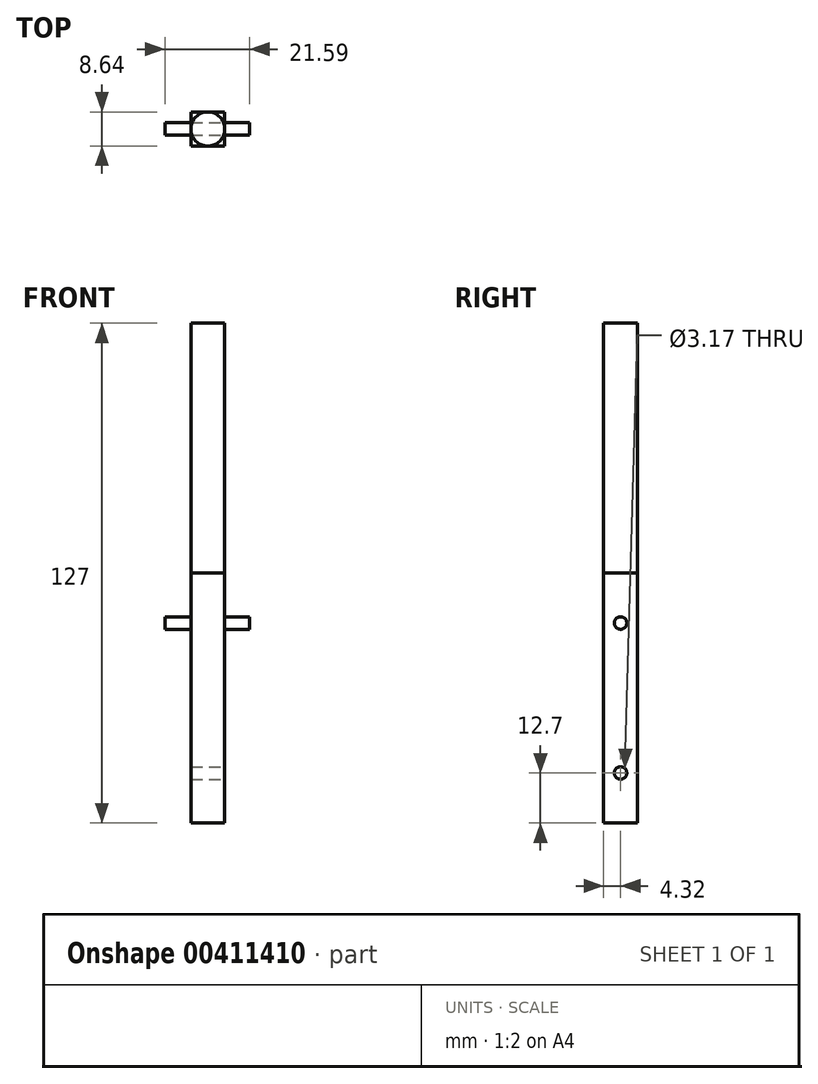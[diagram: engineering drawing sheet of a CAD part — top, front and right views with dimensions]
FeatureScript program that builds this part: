
annotation { "Feature Type Name" : "Feature", "Feature Type Description" : "" }
export const myFeature = defineFeature(function(context is Context, id is Id, definition is map)
    precondition{}
    {
        {
            var Q0;
            Q0=qCreatedBy(makeId("Top.planeOp"),FACE);
            var sketch = newSketch(context, id + "F0", { "sketchPlane" : qUnion([Q0])});
            skLineSegment(sketch, "E0.bottom", {"start": v(-4.32, 4.32) * mm, "end": v(4.32, 4.32) * mm});
            skLineSegment(sketch, "E0.top", {"start": v(-4.32, -4.32) * mm, "end": v(4.32, -4.32) * mm});
            skLineSegment(sketch, "E0.left", {"start": v(-4.32, 4.32) * mm, "end": v(-4.32, -4.32) * mm});
            skLineSegment(sketch, "E0.right", {"start": v(4.32, 4.32) * mm, "end": v(4.32, -4.32) * mm});
            skSolve(sketch);
        }
        {
            var Q0;
            Q0 = qSketchRegion(id + "F0", true);
            extrude(context, id + "F1", {"entities" : qUnion([Q0]), "depth" : 63.5 * mm});
        }
        {
            var Q0;
            Q0=makeQuery(id+"F1.opExtrude","CAP_FACE",FACE,{"disambiguationData":[OSD([sQuery(id+"F0.wireOp",EDGE,"E0.bottom"),sQuery(id+"F0.wireOp",EDGE,"E0.top"),sQuery(id+"F0.wireOp",EDGE,"E0.left"),sQuery(id+"F0.wireOp",EDGE,"E0.right")])],"isStart":false});
            var sketch = newSketch(context, id + "F2", { "sketchPlane" : qUnion([Q0])});
            skCircle(sketch, "E1", {"center": v(0, 0) * mm, "radius": 4.32 * mm});
            skSolve(sketch);
        }
        {
            var Q0;
            Q0 = qSketchRegion(id + "F2", true);
            extrude(context, id + "F3", {"entities" : qUnion([Q0]), "operationType" : NewBodyOperationType.ADD, "depth" : 63.5 * mm});
        }
        {
            var Q0;
            Q0=makeQuery(id+"F1.opExtrude","SWEPT_FACE",FACE,{"disambiguationData":[OSD([sQuery(id+"F0.wireOp",EDGE,"E0.right")])]});
            var sketch = newSketch(context, id + "F4", { "sketchPlane" : qUnion([Q0])});
            skCircle(sketch, "E2", {"center": v(0, 12.7) * mm, "radius": 1.59 * mm});
            skSolve(sketch);
        }
        {
            var Q0;
            Q0 = qSketchRegion(id + "F4", true);
            extrude(context, id + "F5", {"entities" : qUnion([Q0]), "operationType" : NewBodyOperationType.REMOVE, "oppositeDirection" : true, "depth" : 25.4 * mm});
        }
        {
            var Q0;
            Q0=makeQuery(id+"F1.opExtrude","SWEPT_FACE",FACE,{"disambiguationData":[OSD([sQuery(id+"F0.wireOp",EDGE,"E0.right")])]});
            var sketch = newSketch(context, id + "F6", { "sketchPlane" : qUnion([Q0])});
            skCircle(sketch, "E3", {"center": v(0, 50.8) * mm, "radius": 1.59 * mm});
            skSolve(sketch);
        }
        {
            var Q0;
            Q0 = qSketchRegion(id + "F6", true);
            extrude(context, id + "F7", {"entities" : qUnion([Q0]), "operationType" : NewBodyOperationType.ADD, "depth" : 6.35 * mm, "hasSecondDirection" : true, "secondDirectionOppositeDirection" : true, "secondDirectionDepth" : 15.24 * mm});
        }
    });
